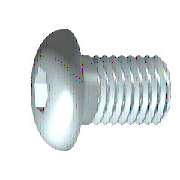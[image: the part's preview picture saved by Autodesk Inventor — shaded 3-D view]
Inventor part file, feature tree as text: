
AUTODESK INVENTOR PART (.ipt)
format: ipt  version: 2023.4 (Build 274418000, 418)  size: 192,512 bytes
history: native  units: mm (DEFAULTED — no unit token found)
features: extrude x1, plane x1, fillet x1
ambient origin geometry x7: Origin, YZ Plane, XY Plane, X Axis, Y Axis, Z Axis, Center Point
bodies: Solid1 (feature_tree), Body (feature_tree)
feature tree (3):
  extrude  "Slot"  Depth=16.9416mm
  plane  "Work Plane1"
  fillet  "Fillet2"  Radius=2.1083mm
